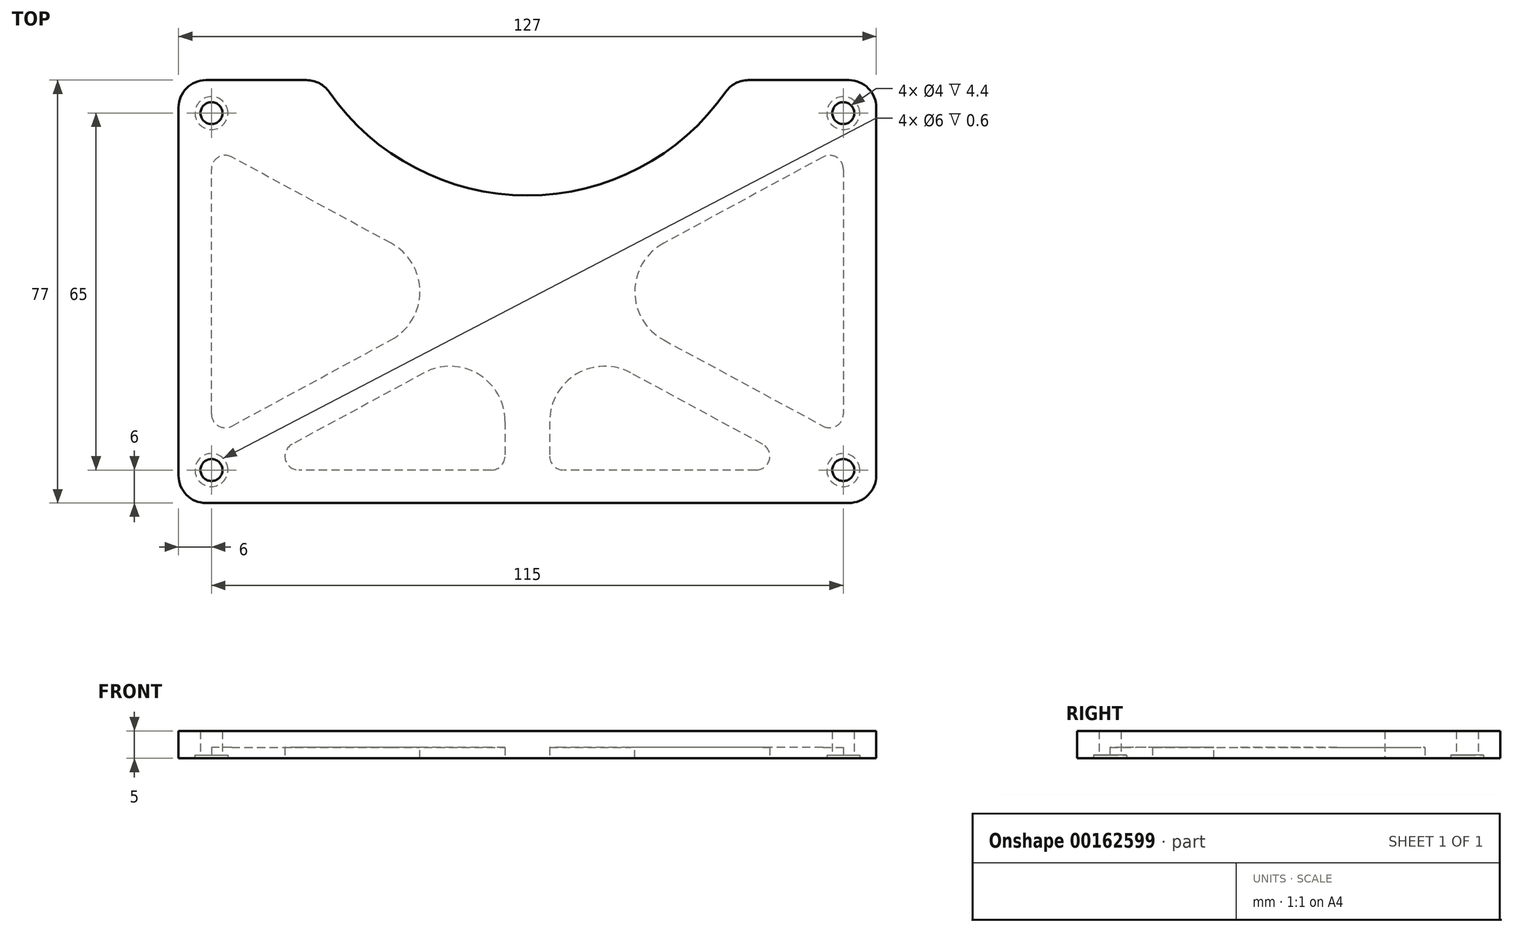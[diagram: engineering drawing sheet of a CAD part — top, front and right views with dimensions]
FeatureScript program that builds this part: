
annotation { "Feature Type Name" : "Feature", "Feature Type Description" : "" }
export const myFeature = defineFeature(function(context is Context, id is Id, definition is map)
    precondition{}
    {
        {
            var Q0;
            Q0=qCreatedBy(makeId("Top.planeOp"),FACE);
            var sketch = newSketch(context, id + "F0", { "sketchPlane" : qUnion([Q0])});
            skLineSegment(sketch, "E0.top", {"start": v(58.5, -38.5) * mm, "end": v(-58.5, -38.5) * mm});
            skLineSegment(sketch, "E0.left", {"start": v(63.5, 33.5) * mm, "end": v(63.5, -33.5) * mm});
            skLineSegment(sketch, "E0.right", {"start": v(-63.5, 33.5) * mm, "end": v(-63.5, -33.5) * mm});
            skPoint(sketch, "E0.middle", {"position": v(0, 0) * mm});
            skLineSegment(sketch, "E1.bottom", {"start": v(57.5, 32.5) * mm, "end": v(-57.5, 32.5) * mm, "construction": true});
            skLineSegment(sketch, "E1.top", {"start": v(57.5, -32.5) * mm, "end": v(-57.5, -32.5) * mm, "construction": true});
            skLineSegment(sketch, "E1.left", {"start": v(57.5, 32.5) * mm, "end": v(57.5, -32.5) * mm, "construction": true});
            skLineSegment(sketch, "E1.right", {"start": v(-57.5, 32.5) * mm, "end": v(-57.5, -32.5) * mm, "construction": true});
            skCircle(sketch, "E2", {"center": v(-57.5, 32.5) * mm, "radius": 2 * mm});
            skCircle(sketch, "E3", {"center": v(57.5, 32.5) * mm, "radius": 2 * mm});
            skCircle(sketch, "E4", {"center": v(57.5, -32.5) * mm, "radius": 2 * mm});
            skCircle(sketch, "E5", {"center": v(-57.5, -32.5) * mm, "radius": 2 * mm});
            skArc(sketch, "E6", {"start": v(-36.1, 36.36) * mm, "mid": v(0, 17.5) * mm, "end": v(36.1, 36.36) * mm});
            skLineSegment(sketch, "E7", {"start": v(58.5, 38.5) * mm, "end": v(40.2, 38.5) * mm});
            skLineSegment(sketch, "E8", {"start": v(-40.2, 38.5) * mm, "end": v(-58.5, 38.5) * mm});
            skPoint(sketch, "E9", {"position": v(0, 17.5) * mm});
            skLineSegment(sketch, "E10", {"start": v(57.5, -38.5) * mm, "end": v(57.5, -34.5) * mm, "construction": true});
            skLineSegment(sketch, "E11", {"start": v(59.5, -32.5) * mm, "end": v(63.5, -32.5) * mm, "construction": true});
            skPoint(sketch, "E12.visualSharp", {"position": v(-63.5, 38.5) * mm});
            skArc(sketch, "E12.filletArc", {"start": v(-58.5, 38.5) * mm, "mid": v(-62.04, 37.04) * mm, "end": v(-63.5, 33.5) * mm});
            skPoint(sketch, "E13.visualSharp", {"position": v(-63.5, -38.5) * mm});
            skArc(sketch, "E13.filletArc", {"start": v(-63.5, -33.5) * mm, "mid": v(-62.04, -37.04) * mm, "end": v(-58.5, -38.5) * mm});
            skPoint(sketch, "E14.visualSharp", {"position": v(63.5, 38.5) * mm});
            skArc(sketch, "E14.filletArc", {"start": v(63.5, 33.5) * mm, "mid": v(62.04, 37.04) * mm, "end": v(58.5, 38.5) * mm});
            skPoint(sketch, "E15.visualSharp", {"position": v(63.5, -38.5) * mm});
            skArc(sketch, "E15.filletArc", {"start": v(58.5, -38.5) * mm, "mid": v(62.04, -37.04) * mm, "end": v(63.5, -33.5) * mm});
            skPoint(sketch, "E16.visualSharp", {"position": v(37.5, 38.5) * mm});
            skArc(sketch, "E16.filletArc", {"start": v(40.2, 38.5) * mm, "mid": v(37.89, 37.93) * mm, "end": v(36.1, 36.36) * mm});
            skPoint(sketch, "E17.visualSharp", {"position": v(-37.5, 38.5) * mm});
            skArc(sketch, "E17.filletArc", {"start": v(-36.1, 36.36) * mm, "mid": v(-37.89, 37.93) * mm, "end": v(-40.2, 38.5) * mm});
            skSolve(sketch);
        }
        {
            var Q0;
            Q0 = qSketchRegion(id + "F0", true);
            extrude(context, id + "F1", {"entities" : qUnion([Q0]), "depth" : 5 * mm});
        }
        {
            var Q0;
            Q0=makeQuery(id+"F1.opExtrude","CAP_FACE",FACE,{"disambiguationData":[OSD([sQuery(id+"F0.wireOp",EDGE,"E0.top"),sQuery(id+"F0.wireOp",EDGE,"E0.left"),sQuery(id+"F0.wireOp",EDGE,"E0.right"),sQuery(id+"F0.wireOp",EDGE,"E2"),sQuery(id+"F0.wireOp",EDGE,"E3"),sQuery(id+"F0.wireOp",EDGE,"E4"),sQuery(id+"F0.wireOp",EDGE,"E5"),sQuery(id+"F0.wireOp",EDGE,"E6"),sQuery(id+"F0.wireOp",EDGE,"E7"),sQuery(id+"F0.wireOp",EDGE,"E8"),sQuery(id+"F0.wireOp",EDGE,"E12.filletArc"),sQuery(id+"F0.wireOp",EDGE,"E13.filletArc"),sQuery(id+"F0.wireOp",EDGE,"E14.filletArc"),sQuery(id+"F0.wireOp",EDGE,"E15.filletArc"),sQuery(id+"F0.wireOp",EDGE,"E16.filletArc"),sQuery(id+"F0.wireOp",EDGE,"E17.filletArc")])],"isStart":true});
            var sketch = newSketch(context, id + "F2", { "sketchPlane" : qUnion([Q0])});
            skCircle(sketch, "E18", {"center": v(-57.5, 32.5) * mm, "radius": 3 * mm});
            skCircle(sketch, "E19", {"center": v(57.5, 32.5) * mm, "radius": 3 * mm});
            skCircle(sketch, "E20", {"center": v(57.5, -32.5) * mm, "radius": 3 * mm});
            skCircle(sketch, "E21", {"center": v(-57.5, -32.5) * mm, "radius": 3 * mm});
            skSolve(sketch);
        }
        {
            var Q0;
            Q0 = qSketchRegion(id + "F2", true);
            extrude(context, id + "F3", {"entities" : qUnion([Q0]), "operationType" : NewBodyOperationType.REMOVE, "oppositeDirection" : true, "depth" : .6 * mm});
        }
        {
            var Q0;
            Q0=makeQuery(id+"F1.opExtrude","CAP_FACE",FACE,{"disambiguationData":[OSD([sQuery(id+"F0.wireOp",EDGE,"E0.top"),sQuery(id+"F0.wireOp",EDGE,"E0.left"),sQuery(id+"F0.wireOp",EDGE,"E0.right"),sQuery(id+"F0.wireOp",EDGE,"E2"),sQuery(id+"F0.wireOp",EDGE,"E3"),sQuery(id+"F0.wireOp",EDGE,"E4"),sQuery(id+"F0.wireOp",EDGE,"E5"),sQuery(id+"F0.wireOp",EDGE,"E6"),sQuery(id+"F0.wireOp",EDGE,"E7"),sQuery(id+"F0.wireOp",EDGE,"E8"),sQuery(id+"F0.wireOp",EDGE,"E12.filletArc"),sQuery(id+"F0.wireOp",EDGE,"E13.filletArc"),sQuery(id+"F0.wireOp",EDGE,"E14.filletArc"),sQuery(id+"F0.wireOp",EDGE,"E15.filletArc"),sQuery(id+"F0.wireOp",EDGE,"E16.filletArc"),sQuery(id+"F0.wireOp",EDGE,"E17.filletArc")])],"isStart":true});
            var sketch = newSketch(context, id + "F4", { "sketchPlane" : qUnion([Q0])});
            skArc(sketch, "E22", {"start": v(-57.5, 26.5) * mm, "mid": v(-53.26, 28.26) * mm, "end": v(-51.5, 32.5) * mm});
            skArc(sketch, "E23", {"start": v(-51.5, -32.5) * mm, "mid": v(-53.26, -28.26) * mm, "end": v(-57.5, -26.5) * mm});
            skArc(sketch, "E24", {"start": v(51.5, 32.5) * mm, "mid": v(53.26, 28.26) * mm, "end": v(57.5, 26.5) * mm});
            skArc(sketch, "E25", {"start": v(57.5, -26.5) * mm, "mid": v(53.26, -28.26) * mm, "end": v(51.5, -32.5) * mm});
            skLineSegment(sketch, "E26", {"start": v(57.5, -26.5) * mm, "end": v(57.5, 26.5) * mm});
            skLineSegment(sketch, "E27", {"start": v(51.5, 32.5) * mm, "end": v(-51.5, 32.5) * mm});
            skLineSegment(sketch, "E28", {"start": v(-57.5, 26.5) * mm, "end": v(-57.5, -26.5) * mm});
            skLineSegment(sketch, "E29", {"start": v(-51.5, -32.5) * mm, "end": v(-40.72, -32.5) * mm});
            skLineSegment(sketch, "E30", {"start": v(51.5, -32.5) * mm, "end": v(40.72, -32.5) * mm});
            skArc(sketch, "E31", {"start": v(40.72, -32.5) * mm, "mid": v(0, -11.5) * mm, "end": v(-40.72, -32.5) * mm});
            skLineSegment(sketch, "E32", {"start": v(0, 32.5) * mm, "end": v(0, 38.5) * mm, "construction": true});
            skLineSegment(sketch, "E33", {"start": v(57.5, 0) * mm, "end": v(63.5, 0) * mm, "construction": true});
            skPoint(sketch, "E33.endSnap0", {"position": v(57.5, 0) * mm});
            skLineSegment(sketch, "E34", {"start": v(-57.5, 0) * mm, "end": v(-63.5, 0) * mm, "construction": true});
            skLineSegment(sketch, "E35", {"start": v(0, -17.5) * mm, "end": v(0, -11.5) * mm, "construction": true});
            skLineSegment(sketch, "E36", {"start": v(49.35, -38.5) * mm, "end": v(49.35, -32.5) * mm, "construction": true});
            skLineSegment(sketch, "E37", {"start": v(-51.5, -32.5) * mm, "end": v(57.5, 26.5) * mm});
            skLineSegment(sketch, "E38", {"start": v(51.5, 32.5) * mm, "end": v(-57.5, -26.5) * mm});
            skLineSegment(sketch, "E39", {"start": v(57.5, -26.5) * mm, "end": v(-51.5, 32.5) * mm});
            skLineSegment(sketch, "E40", {"start": v(-57.5, 26.5) * mm, "end": v(51.5, -32.5) * mm});
            skLineSegment(sketch, "E41", {"start": v(-4.07, 6.82) * mm, "end": v(-4.07, 32.5) * mm});
            skLineSegment(sketch, "E42", {"start": v(4.07, 6.82) * mm, "end": v(4.07, 32.5) * mm});
            skLineSegment(sketch, "E43", {"start": v(-4.07, 19.66) * mm, "end": v(4.07, 19.66) * mm, "construction": true});
            skLineSegment(sketch, "E44", {"start": v(-21.4, 16.2) * mm, "end": v(-25.27, 9.06) * mm, "construction": true});
            skSolve(sketch);
        }
        {
            var Q0;
            {var subQ0=sQuery(id+"F4.wireOp",EDGE,"E28");Q0=makeQuery(id+"F4.imprint","IMPRINT",FACE,{"disambiguationData":[TD([[makeQuery(id+"F4.imprint","IMPRINT",EDGE,{"derivedFrom":subQ0}),1.0]])]});}
            var Q1;
            {var subQ0=sQuery(id+"F4.wireOp",EDGE,"E27");Q1=makeQuery(id+"F4.imprint","IMPRINT",FACE,{"disambiguationData":[TD([[makeQuery(id+"F4.imprint","IMPRINT",EDGE,{"derivedFrom":subQ0}),1.0]])]});}
            var Q2;
            {var subQ0=sQuery(id+"F4.wireOp",EDGE,"E26");Q2=makeQuery(id+"F4.imprint","IMPRINT",FACE,{"disambiguationData":[TD([[makeQuery(id+"F4.imprint","IMPRINT",EDGE,{"derivedFrom":subQ0}),1.0]])]});}
            extrude(context, id + "F5", {"entities" : qUnion([Q0, Q1, Q2]), "operationType" : NewBodyOperationType.REMOVE, "oppositeDirection" : true, "depth" : 2 * mm});
        }
        {
            var Q0;
            Q0=makeQuery(id+"F5.boolean.opBoolean","COPY",EDGE,{"derivedFrom":makeQuery(id+"F5.opExtrude","SWEPT_EDGE",EDGE,{"disambiguationData":[OSD([sQuery(id+"F4.wireOp",EDGE,"E38"),sQuery(id+"F4.wireOp",EDGE,"E39")])]})});
            var Q1;
            Q1=makeQuery(id+"F5.boolean.opBoolean","COPY",EDGE,{"derivedFrom":makeQuery(id+"F5.opExtrude","SWEPT_EDGE",EDGE,{"disambiguationData":[OSD([sQuery(id+"F4.wireOp",EDGE,"E37"),sQuery(id+"F4.wireOp",EDGE,"E39")])]})});
            var Q2;
            Q2=makeQuery(id+"F5.boolean.opBoolean","COPY",EDGE,{"derivedFrom":makeQuery(id+"F5.opExtrude","SWEPT_EDGE",EDGE,{"disambiguationData":[OSD([sQuery(id+"F4.wireOp",EDGE,"E38"),sQuery(id+"F4.wireOp",EDGE,"E40")])]})});
            var Q3;
            Q3=makeQuery(id+"F5.boolean.opBoolean","COPY",EDGE,{"derivedFrom":makeQuery(id+"F5.opExtrude","SWEPT_EDGE",EDGE,{"disambiguationData":[OSD([sQuery(id+"F4.wireOp",EDGE,"E37"),sQuery(id+"F4.wireOp",EDGE,"E40")])]})});
            fillet(context, id + "F6", {"entities" : qUnion([Q0, Q1, Q2, Q3]), "radius" : 10 * mm, "tangentPropagation" : true, "allowEdgeOverflow" : false});
        }
        {
            var Q0;
            Q0=makeQuery(id+"F5.boolean.opBoolean","COPY",EDGE,{"derivedFrom":makeQuery(id+"F5.opExtrude","SWEPT_EDGE",EDGE,{"disambiguationData":[OSD([sQuery(id+"F4.wireOp",EDGE,"E22"),sQuery(id+"F4.wireOp",EDGE,"E27"),sQuery(id+"F4.wireOp",EDGE,"E39")])]})});
            var Q1;
            Q1=makeQuery(id+"F5.boolean.opBoolean","COPY",EDGE,{"derivedFrom":makeQuery(id+"F5.opExtrude","SWEPT_EDGE",EDGE,{"disambiguationData":[OSD([sQuery(id+"F4.wireOp",EDGE,"E24"),sQuery(id+"F4.wireOp",EDGE,"E27"),sQuery(id+"F4.wireOp",EDGE,"E38")])]})});
            var Q2;
            Q2=makeQuery(id+"F5.boolean.opBoolean","COPY",EDGE,{"derivedFrom":makeQuery(id+"F5.opExtrude","SWEPT_EDGE",EDGE,{"disambiguationData":[OSD([sQuery(id+"F4.wireOp",EDGE,"E24"),sQuery(id+"F4.wireOp",EDGE,"E26"),sQuery(id+"F4.wireOp",EDGE,"E37")])]})});
            var Q3;
            Q3=makeQuery(id+"F5.boolean.opBoolean","COPY",EDGE,{"derivedFrom":makeQuery(id+"F5.opExtrude","SWEPT_EDGE",EDGE,{"disambiguationData":[OSD([sQuery(id+"F4.wireOp",EDGE,"E25"),sQuery(id+"F4.wireOp",EDGE,"E26"),sQuery(id+"F4.wireOp",EDGE,"E39")])]})});
            var Q4;
            Q4=makeQuery(id+"F5.boolean.opBoolean","COPY",EDGE,{"derivedFrom":makeQuery(id+"F5.opExtrude","SWEPT_EDGE",EDGE,{"disambiguationData":[OSD([sQuery(id+"F4.wireOp",EDGE,"E23"),sQuery(id+"F4.wireOp",EDGE,"E28"),sQuery(id+"F4.wireOp",EDGE,"E38")])]})});
            var Q5;
            Q5=makeQuery(id+"F5.boolean.opBoolean","COPY",EDGE,{"derivedFrom":makeQuery(id+"F5.opExtrude","SWEPT_EDGE",EDGE,{"disambiguationData":[OSD([sQuery(id+"F4.wireOp",EDGE,"E22"),sQuery(id+"F4.wireOp",EDGE,"E28"),sQuery(id+"F4.wireOp",EDGE,"E40")])]})});
            var Q6;
            Q6=makeQuery(id+"F5.boolean.opBoolean","COPY",EDGE,{"derivedFrom":makeQuery(id+"F5.opExtrude","SWEPT_EDGE",EDGE,{"disambiguationData":[OSD([sQuery(id+"F4.wireOp",EDGE,"E30"),sQuery(id+"F4.wireOp",EDGE,"E31")])]})});
            var Q7;
            Q7=makeQuery(id+"F5.boolean.opBoolean","COPY",EDGE,{"derivedFrom":makeQuery(id+"F5.opExtrude","SWEPT_EDGE",EDGE,{"disambiguationData":[OSD([sQuery(id+"F4.wireOp",EDGE,"E29"),sQuery(id+"F4.wireOp",EDGE,"E31")])]})});
            var Q8;
            Q8=makeQuery(id+"F5.boolean.opBoolean","COPY",EDGE,{"derivedFrom":makeQuery(id+"F5.opExtrude","SWEPT_EDGE",EDGE,{"disambiguationData":[OSD([sQuery(id+"F4.wireOp",EDGE,"E27"),sQuery(id+"F4.wireOp",EDGE,"E42")])]})});
            var Q9;
            Q9=makeQuery(id+"F5.boolean.opBoolean","COPY",EDGE,{"derivedFrom":makeQuery(id+"F5.opExtrude","SWEPT_EDGE",EDGE,{"disambiguationData":[OSD([sQuery(id+"F4.wireOp",EDGE,"E27"),sQuery(id+"F4.wireOp",EDGE,"E41")])]})});
            fillet(context, id + "F7", {"entities" : qUnion([Q0, Q1, Q2, Q3, Q4, Q5, Q6, Q7, Q8, Q9]), "radius" : 2.5 * mm, "tangentPropagation" : true, "allowEdgeOverflow" : false});
        }
    });
